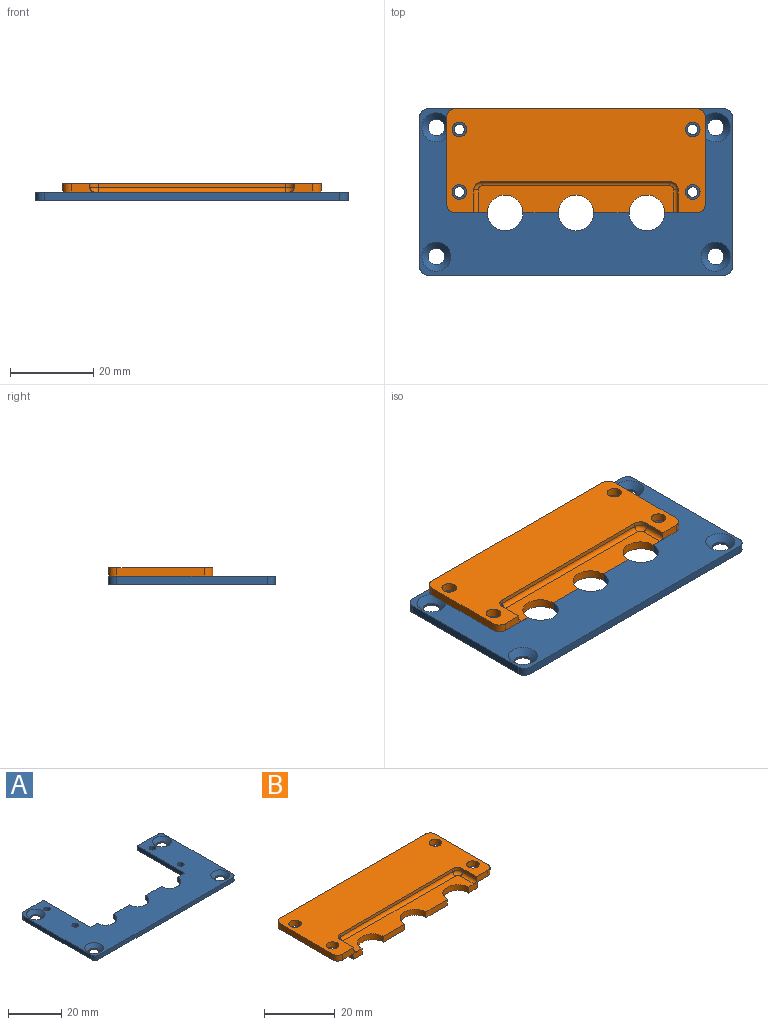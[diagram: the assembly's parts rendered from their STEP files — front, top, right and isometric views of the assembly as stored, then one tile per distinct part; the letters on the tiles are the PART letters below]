
ASSEMBLY  parts=2 mates=1
PART A: 32 faces, bbox 75x40x2 mm
  f0: plane 10.5x2mm, normal (0,1,0), area 21mm2, adj f9,f12,f13,f23
  f1: cylinder r=4.25mm len=8.5mm, axis (0,0,1), area 26.7mm2, adj f12,f13,f18,f22
  f2: cylinder r=4.25mm len=8.5mm, axis (0,0,1), area 26.7mm2, adj f12,f13,f18,f19
  f3: cylinder r=4.25mm len=8.5mm, axis (0,0,1), area 26.7mm2, adj f12,f13,f19,f20
  f4: plane 36x2mm, normal (-1,0,0), area 72mm2, adj f5,f11,f12,f13
  f5: cylinder r=2mm len=2mm, axis (0,0,1), area 6.3mm2, adj f4,f6,f12,f13
  f6: plane 71x2mm, normal (0,-1,0), area 142mm2, adj f5,f7,f12,f13
  f7: cylinder r=2mm len=2mm, axis (0,0,1), area 6.3mm2, adj f6,f8,f12,f13
  f8: plane 36x2mm, normal (1,0,0), area 72mm2, adj f7,f9,f12,f13
  f9: cylinder r=2mm len=2mm, axis (0,0,1), area 6.3mm2, adj f0,f8,f12,f13
  f10: plane 10.5x2mm, normal (0,1,0), area 21mm2, adj f11,f12,f13,f21
  f11: cylinder r=2mm len=2mm, axis (0,0,1), area 6.3mm2, adj f4,f10,f12,f13
  f12: plane 75x40mm, normal (0,0,1), area 1487.9mm2, adj f0,f1,f2,f3,f4,f5,f6,f7
  f13: plane 75x40mm, normal (0,0,-1), area 1591.5mm2, adj f0,f1,f2,f3,f4,f5,f6,f7
  f14: cylinder r=2mm len=4mm, axis (0,0,1), area 6.3mm2, adj f13,f31
  f15: cylinder r=2mm len=4mm, axis (0,0,1), area 6.3mm2, adj f13,f30
  f16: cylinder r=2mm len=4mm, axis (0,0,1), area 6.3mm2, adj f13,f29
  f17: cylinder r=2mm len=4mm, axis (0,0,1), area 6.3mm2, adj f13,f28
  f18: plane 8.5x2mm, normal (0,1,0), area 17mm2, adj f1,f2,f12,f13
  f19: plane 8.5x2mm, normal (0,1,0), area 17mm2, adj f2,f3,f12,f13
  f20: plane 3.75x2mm, normal (0,1,0), area 7.5mm2, adj f3,f12,f13,f21
  f21: plane 25x2mm, normal (1,0,0), area 50mm2, adj f10,f12,f13,f20
  f22: plane 3.75x2mm, normal (0,1,0), area 7.5mm2, adj f1,f12,f13,f23
  f23: plane 25x2mm, normal (-1,0,0), area 50mm2, adj f0,f12,f13,f22
  f24: cylinder r=1.25mm len=2.5mm, axis (0,0,1), area 15.7mm2, adj f12,f13
  f25: cylinder r=1.25mm len=2.5mm, axis (0,0,1), area 15.7mm2, adj f12,f13
  f26: cylinder r=1.25mm len=2.5mm, axis (0,0,1), area 15.7mm2, adj f12,f13
  f27: cylinder r=1.25mm len=2.5mm, axis (0,0,1), area 15.7mm2, adj f12,f13
  f28: cone r=2mm half-angle=45deg, axis (0,0,1), area 36.7mm2, adj f12,f17
  f29: cone r=2mm half-angle=45deg, axis (0,0,1), area 36.7mm2, adj f12,f16
  f30: cone r=2mm half-angle=45deg, axis (0,0,1), area 36.7mm2, adj f12,f15
  f31: cone r=2mm half-angle=45deg, axis (0,0,1), area 36.7mm2, adj f12,f14
PART B: 35 faces, bbox 62x25x4 mm
  f0: plane 7.75x4mm, normal (0,-1,0), area 16.2mm2, adj f4,f9,f13,f19,f21,f25,f26,f27
  f1: plane 7.75x4mm, normal (0,-1,0), area 16.2mm2, adj f4,f10,f13,f18,f22,f25,f28,f29
  f2: plane 58x4mm, normal (0,1,0), area 215mm2, adj f4,f11,f12,f13,f26,f27,f28,f29
  f3: plane 21x2mm, normal (-1,0,0), area 42mm2, adj f9,f12,f13,f27
  f4: plane 49.5x25mm, normal (0,0,-1), area 1152.4mm2, adj f0,f1,f2,f14,f15,f17,f18,f19
  f5: cylinder r=1.75mm len=3.5mm, axis (0,0,1), area 22mm2, adj f13,f27
  f6: cylinder r=1.75mm len=3.5mm, axis (0,0,1), area 22mm2, adj f13,f27
  f7: cylinder r=1.75mm len=3.5mm, axis (0,0,1), area 22mm2, adj f13,f29
  f8: cylinder r=1.75mm len=3.5mm, axis (0,0,1), area 22mm2, adj f13,f29
  f9: cylinder r=2mm len=2mm, axis (0,0,1), area 6.3mm2, adj f0,f3,f13,f27
  f10: cylinder r=2mm len=2mm, axis (0,0,-1), area 6.3mm2, adj f1,f13,f16,f29
  f11: cylinder r=2mm len=2mm, axis (0,0,1), area 6.3mm2, adj f2,f13,f16,f29
  f12: cylinder r=2mm len=2mm, axis (0,0,-1), area 6.3mm2, adj f2,f3,f13,f27
  f13: plane 62x25mm, normal (0,0,1), area 1142.3mm2, adj f0,f1,f2,f3,f5,f6,f7,f8
  f14: plane 8.5x2mm, normal (0,-1,0), area 17mm2, adj f4,f17,f18,f25
  f15: plane 8.5x2mm, normal (0,-1,0), area 17mm2, adj f4,f17,f19,f25
  f16: plane 21x2mm, normal (1,0,0), area 42mm2, adj f10,f11,f13,f29
  f17: cylinder r=4.25mm len=8.5mm, axis (0,0,1), area 26.7mm2, adj f4,f14,f15,f25
  f18: cylinder r=4.25mm len=8.5mm, axis (0,0,1), area 26.7mm2, adj f1,f4,f14,f25
  f19: cylinder r=4.25mm len=8.5mm, axis (0,0,1), area 26.7mm2, adj f0,f4,f15,f25
  f20: cylinder r=2mm len=2mm, axis (0,0,1), area 3.1mm2, adj f13,f21,f24,f33
  f21: plane 5.5x1mm, normal (1,0,0), area 5.5mm2, adj f0,f13,f20,f34
  f22: plane 5.5x1mm, normal (-1,0,0), area 5.5mm2, adj f1,f13,f23,f30
  f23: cylinder r=2mm len=2mm, axis (0,0,1), area 3.1mm2, adj f13,f22,f24,f31
  f24: plane 45x1mm, normal (0,-1,0), area 45mm2, adj f13,f20,f23,f32
  f25: plane 47x6.5mm, normal (0,0,1), area 220mm2, adj f0,f1,f14,f15,f17,f18,f19,f30
  f26: plane 25x2mm, normal (-1,0,0), area 50mm2, adj f0,f2,f4,f27
  f27: plane 25x6.25mm, normal (0,0,-1), area 135.3mm2, adj f0,f2,f3,f5,f6,f9,f12,f26
  f28: plane 25x2mm, normal (1,0,0), area 50mm2, adj f1,f2,f4,f29
  f29: plane 25x6.25mm, normal (0,0,-1), area 135.3mm2, adj f1,f2,f7,f8,f10,f11,f16,f28
  f30: cylinder r=1mm len=5.5mm, axis (0,1,0), area 8.6mm2, adj f1,f22,f25,f31
  f31: torus R=1mm, axis (0,0,1), area 4mm2, adj f23,f25,f30,f32
  f32: cylinder r=1mm len=45mm, axis (-1,0,0), area 70.7mm2, adj f24,f25,f31,f33
  f33: torus R=1mm, axis (0,0,1), area 4mm2, adj f20,f25,f32,f34
  f34: cylinder r=1mm len=5.5mm, axis (0,-1,0), area 8.6mm2, adj f0,f21,f25,f33
PLACE A t=(0,-8.29,0)mm
PLACE B t=(0,-0.79,0)mm
MATE fastened A.f26 <-> B.f8  axis (0,0,1) through (28,6.71,2)mm
